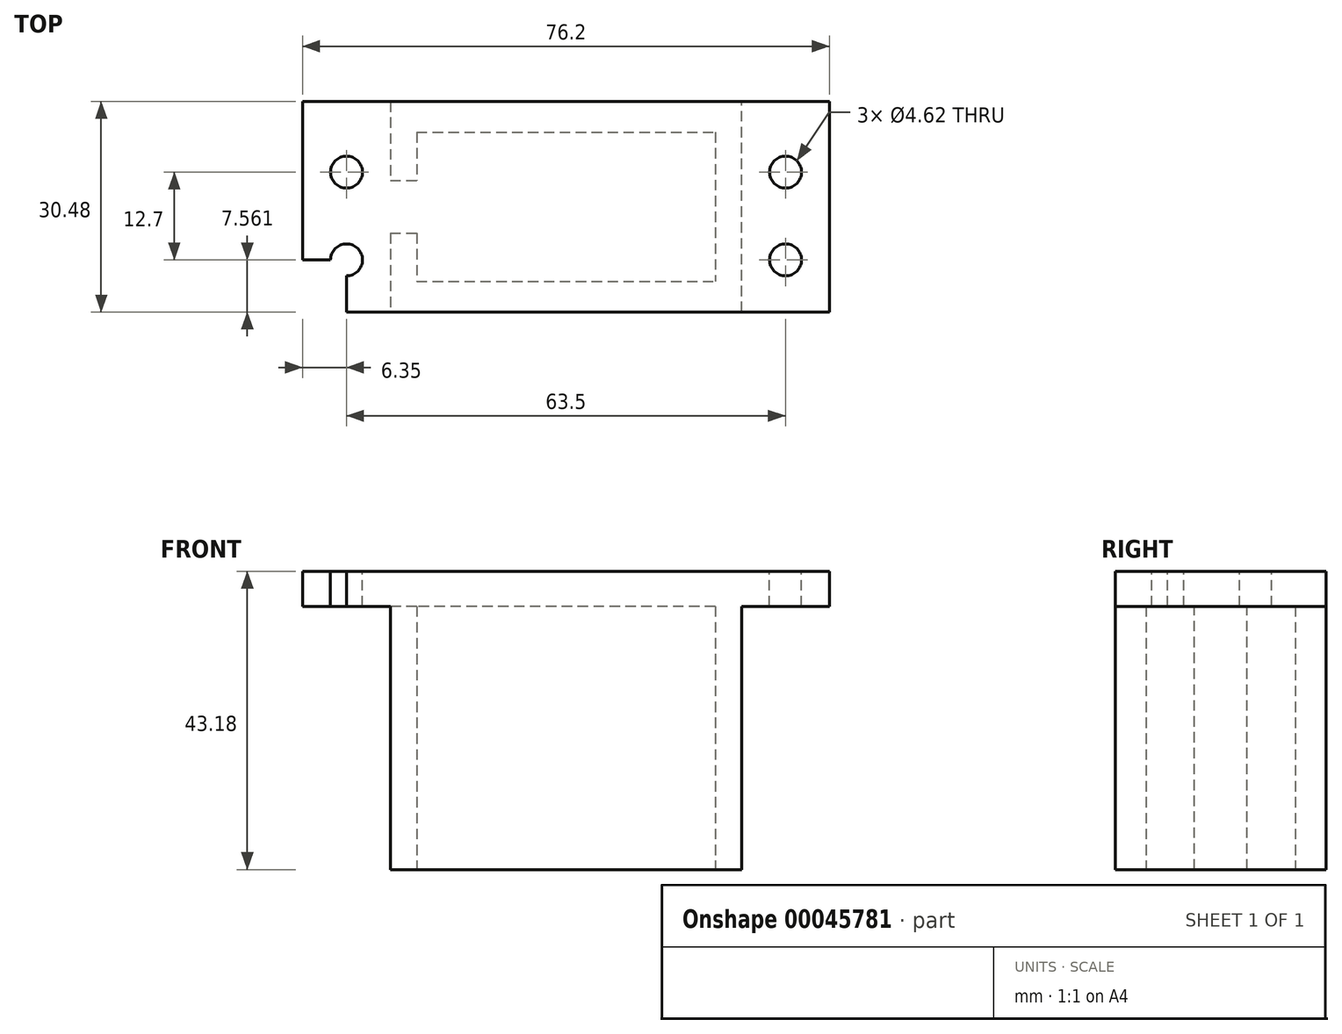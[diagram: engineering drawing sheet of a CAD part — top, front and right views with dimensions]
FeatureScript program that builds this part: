
annotation { "Feature Type Name" : "Feature", "Feature Type Description" : "" }
export const myFeature = defineFeature(function(context is Context, id is Id, definition is map)
    precondition{}
    {
        {
            var Q0;
            Q0=qCreatedBy(makeId("Top.planeOp"),FACE);
            var sketch = newSketch(context, id + "F0", { "sketchPlane" : qUnion([Q0])});
            skLineSegment(sketch, "E0.rect.bottom", {"start": v(25.4, -15.24) * mm, "end": v(-25.4, -15.24) * mm});
            skLineSegment(sketch, "E0.rect.top", {"start": v(25.4, 15.24) * mm, "end": v(-25.4, 15.24) * mm});
            skLineSegment(sketch, "E0.rect.left", {"start": v(25.4, -15.24) * mm, "end": v(25.4, 15.24) * mm});
            skLineSegment(sketch, "E0.rect.right", {"start": v(-25.4, -15.24) * mm, "end": v(-25.4, 15.24) * mm});
            skPoint(sketch, "E0.rect.middle", {"position": v(0, 0) * mm});
            skSolve(sketch);
        }
        {
            var Q0;
            Q0=makeQuery(id+"F0.imprint","IMPRINT",FACE,{"disambiguationData":[TD([[makeQuery(id+"F0.imprint","IMPRINT",EDGE,{"derivedFrom":sQuery(id+"F0.wireOp",EDGE,"E0.rect.bottom")}),-1.0]])]});
            extrude(context, id + "F1", {"entities" : qUnion([Q0]), "depth" : 50.8 * mm});
        }
        {
            var Q0;
            Q0=qCreatedBy(makeId("Top.planeOp"),FACE);
            var sketch = newSketch(context, id + "F2", { "sketchPlane" : qUnion([Q0])});
            skLineSegment(sketch, "E1.rect.bottom", {"start": v(21.59, -10.8) * mm, "end": v(-21.59, -10.8) * mm});
            skLineSegment(sketch, "E1.rect.top", {"start": v(21.59, 10.8) * mm, "end": v(-21.59, 10.8) * mm});
            skLineSegment(sketch, "E1.rect.left", {"start": v(21.59, -10.8) * mm, "end": v(21.59, 10.8) * mm});
            skLineSegment(sketch, "E1.rect.right", {"start": v(-21.59, -10.8) * mm, "end": v(-21.59, 10.8) * mm});
            skPoint(sketch, "E1.rect.middle", {"position": v(0, 0) * mm});
            skSolve(sketch);
        }
        {
            var Q0;
            Q0=makeQuery(id+"F2.imprint","IMPRINT",FACE,{"disambiguationData":[TD([[makeQuery(id+"F2.imprint","IMPRINT",EDGE,{"derivedFrom":sQuery(id+"F2.wireOp",EDGE,"E1.rect.bottom")}),-1.0]])]});
            extrude(context, id + "F3", {"entities" : qUnion([Q0]), "operationType" : NewBodyOperationType.REMOVE, "depth" : 45.72 * mm});
        }
        {
            var Q0;
            Q0=makeQuery(id+"F1.opExtrude","CAP_FACE",FACE,{"disambiguationData":[OSD([sQuery(id+"F0.wireOp",EDGE,"E0.rect.bottom"),sQuery(id+"F0.wireOp",EDGE,"E0.rect.top"),sQuery(id+"F0.wireOp",EDGE,"E0.rect.left"),sQuery(id+"F0.wireOp",EDGE,"E0.rect.right")])],"isStart":false});
            var sketch = newSketch(context, id + "F4", { "sketchPlane" : qUnion([Q0])});
            skLineSegment(sketch, "E2.bottom", {"start": v(25.4, 15.24) * mm, "end": v(38.1, 15.24) * mm});
            skLineSegment(sketch, "E2.top", {"start": v(25.4, -15.24) * mm, "end": v(38.1, -15.24) * mm});
            skLineSegment(sketch, "E2.left", {"start": v(25.4, 15.24) * mm, "end": v(25.4, -15.24) * mm});
            skLineSegment(sketch, "E2.right", {"start": v(38.1, 15.24) * mm, "end": v(38.1, -15.24) * mm});
            skLineSegment(sketch, "E3.bottom", {"start": v(-25.4, 15.24) * mm, "end": v(-38.1, 15.24) * mm});
            skLineSegment(sketch, "E3.top", {"start": v(-25.4, -15.24) * mm, "end": v(-38.1, -15.24) * mm});
            skLineSegment(sketch, "E3.left", {"start": v(-25.4, 15.24) * mm, "end": v(-25.4, -15.24) * mm});
            skLineSegment(sketch, "E3.right", {"start": v(-38.1, 15.24) * mm, "end": v(-38.1, -15.24) * mm});
            skCircle(sketch, "E4", {"center": v(-31.75, 5.02) * mm, "radius": 2.31 * mm});
            skCircle(sketch, "E5", {"center": v(31.75, 5.02) * mm, "radius": 2.31 * mm});
            skCircle(sketch, "E6", {"center": v(-31.75, -7.68) * mm, "radius": 2.31 * mm});
            skCircle(sketch, "E7", {"center": v(31.75, -7.68) * mm, "radius": 2.31 * mm});
            skLineSegment(sketch, "E8", {"start": v(-31.75, 5.02) * mm, "end": v(-31.75, 15.24) * mm});
            skLineSegment(sketch, "E9", {"start": v(-31.75, -7.68) * mm, "end": v(-38.1, -7.68) * mm});
            skLineSegment(sketch, "E10", {"start": v(-31.75, -7.68) * mm, "end": v(-31.75, -15.24) * mm});
            skLineSegment(sketch, "E11", {"start": v(31.75, 5.02) * mm, "end": v(31.75, 15.24) * mm});
            skLineSegment(sketch, "E12", {"start": v(31.75, -7.68) * mm, "end": v(31.75, -15.24) * mm});
            skLineSegment(sketch, "E13", {"start": v(38.1, -15.24) * mm, "end": v(-38.1, -15.24) * mm});
            skSolve(sketch);
        }
        {
            var Q0;
            Q0=makeQuery(id+"F4.imprint","IMPRINT",FACE,{"disambiguationData":[TD([[makeQuery(id+"F4.imprint","IMPRINT",EDGE,{"derivedFrom":sQuery(id+"F4.wireOp",EDGE,"E2.bottom")}),-1.0]])]});
            var Q1;
            Q1=makeQuery(id+"F4.imprint","IMPRINT",FACE,{"disambiguationData":[TD([[makeQuery(id+"F4.imprint","IMPRINT",EDGE,{"derivedFrom":sQuery(id+"F4.wireOp",EDGE,"E3.bottom")}),1.0]])]});
            extrude(context, id + "F5", {"entities" : qUnion([Q0, Q1]), "operationType" : NewBodyOperationType.ADD, "oppositeDirection" : true, "depth" : 5.08 * mm});
        }
        {
            var Q0;
            Q0=makeQuery(id+"F1.opExtrude","SWEPT_FACE",FACE,{"disambiguationData":[OSD([sQuery(id+"F0.wireOp",EDGE,"E0.rect.right")])]});
            var sketch = newSketch(context, id + "F6", { "sketchPlane" : qUnion([Q0])});
            skLineSegment(sketch, "E14.rect.bottom", {"start": v(3.8, -45.72) * mm, "end": v(-3.81, -45.72) * mm});
            skLineSegment(sketch, "E14.rect.top", {"start": v(3.81, 45.72) * mm, "end": v(-3.8, 45.72) * mm});
            skLineSegment(sketch, "E14.rect.left", {"start": v(3.8, -45.72) * mm, "end": v(3.81, 45.72) * mm});
            skLineSegment(sketch, "E14.rect.right", {"start": v(-3.81, -45.72) * mm, "end": v(-3.8, 45.72) * mm});
            skPoint(sketch, "E14.rect.middle", {"position": v(0, 0) * mm});
            skSolve(sketch);
        }
        {
            var Q0;
            {var subQ3=sQuery(id+"F6.wireOp",EDGE,"E14.rect.bottom");Q0=makeQuery(id+"F6.imprint","IMPRINT",FACE,{"disambiguationData":[TD([[makeQuery(id+"F6.imprint","IMPRINT",EDGE,{"derivedFrom":subQ3}),-1.0]])]});}
            var Q1;
            {var subQ6=sQuery(id+"F6.wireOp",EDGE,"E14.rect.top");Q1=makeQuery(id+"F6.imprint","IMPRINT",FACE,{"disambiguationData":[TD([[makeQuery(id+"F6.imprint","IMPRINT",EDGE,{"derivedFrom":subQ6}),1.0]])]});}
            extrude(context, id + "F7", {"entities" : qUnion([Q0, Q1]), "operationType" : NewBodyOperationType.REMOVE, "oppositeDirection" : true, "depth" : 13.47 * mm});
        }
        {
            var Q0;
            Q0=makeQuery(id+"F1.opExtrude","SWEPT_FACE",FACE,{"disambiguationData":[OSD([sQuery(id+"F0.wireOp",EDGE,"E0.rect.left")])]});
            var sketch = newSketch(context, id + "F8", { "sketchPlane" : qUnion([Q0])});
            skLineSegment(sketch, "E15", {"start": v(-15.24, 45.72) * mm, "end": v(-15.24, 7.62) * mm});
            skLineSegment(sketch, "E16.bottom", {"start": v(-15.24, 7.62) * mm, "end": v(26.81, 7.62) * mm});
            skLineSegment(sketch, "E16.top", {"start": v(-15.24, -4.41) * mm, "end": v(26.81, -4.41) * mm});
            skLineSegment(sketch, "E16.left", {"start": v(-15.24, 7.62) * mm, "end": v(-15.24, -4.41) * mm});
            skLineSegment(sketch, "E16.right", {"start": v(26.81, 7.62) * mm, "end": v(26.81, -4.41) * mm});
            skSolve(sketch);
        }
        {
            var Q0;
            {var subQ0=sQuery(id+"F0.wireOp",EDGE,"E0.rect.left");var subQ1=makeQuery(id+"F1.opExtrude","CAP_EDGE",EDGE,{"disambiguationData":[OSD([subQ0])],"isStart":true});Q0=makeQuery(id+"F8.imprint","IMPRINT",FACE,{"disambiguationData":[TD([[makeQuery(id+"F8.imprint","IMPRINT",EDGE,{"derivedFrom":subQ1}),1.0]])]});}
            var Q1;
            {var subQ6=sQuery(id+"F8.wireOp",EDGE,"E16.top");Q1=makeQuery(id+"F8.imprint","IMPRINT",FACE,{"disambiguationData":[TD([[makeQuery(id+"F8.imprint","IMPRINT",EDGE,{"derivedFrom":subQ6}),1.0]])]});}
            extrude(context, id + "F9", {"entities" : qUnion([Q0, Q1]), "operationType" : NewBodyOperationType.REMOVE, "oppositeDirection" : true, "depth" : 78.77 * mm});
        }
    });
